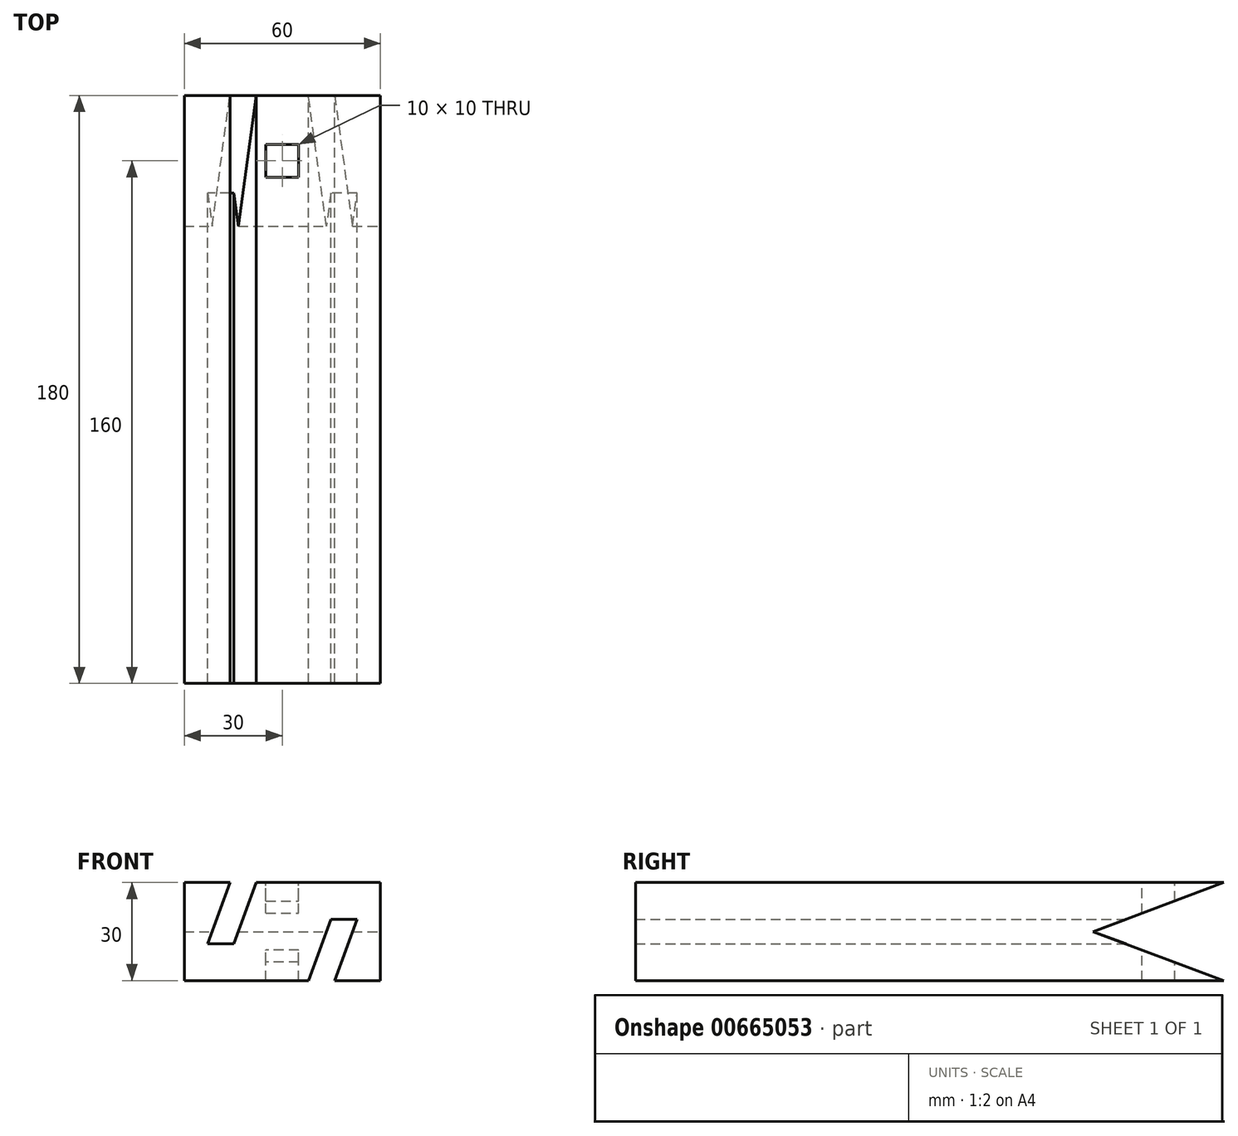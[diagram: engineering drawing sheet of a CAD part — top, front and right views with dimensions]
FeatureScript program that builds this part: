
annotation { "Feature Type Name" : "Feature", "Feature Type Description" : "" }
export const myFeature = defineFeature(function(context is Context, id is Id, definition is map)
    precondition{}
    {
        {
            var Q0;
            Q0=qCreatedBy(makeId("Front.planeOp"),FACE);
            var sketch = newSketch(context, id + "F0", { "sketchPlane" : qUnion([Q0])});
            skLineSegment(sketch, "E0.bottom", {"start": v(30, 15) * mm, "end": v(-30, 15) * mm});
            skLineSegment(sketch, "E0.top", {"start": v(30, -15) * mm, "end": v(-30, -15) * mm});
            skLineSegment(sketch, "E0.left", {"start": v(30, 15) * mm, "end": v(30, -15) * mm});
            skLineSegment(sketch, "E0.right", {"start": v(-30, 15) * mm, "end": v(-30, -15) * mm});
            skLineSegment(sketch, "E1", {"start": v(-8, 15) * mm, "end": v(-14.84, -3.8) * mm});
            skLineSegment(sketch, "E2", {"start": v(-14.84, -3.8) * mm, "end": v(-22.84, -3.8) * mm});
            skLineSegment(sketch, "E3", {"start": v(-22.84, -3.8) * mm, "end": v(-16, 15) * mm});
            skLineSegment(sketch, "E4", {"start": v(16, -15) * mm, "end": v(22.84, 3.8) * mm});
            skLineSegment(sketch, "E5", {"start": v(22.84, 3.8) * mm, "end": v(14.84, 3.8) * mm});
            skLineSegment(sketch, "E6", {"start": v(14.84, 3.8) * mm, "end": v(8, -15) * mm});
            skSolve(sketch);
        }
        {
            var Q0;
            {var subQ3=sQuery(id+"F0.wireOp",EDGE,"E0.left");Q0=makeQuery(id+"F0.imprint","IMPRINT",FACE,{"disambiguationData":[TD([[makeQuery(id+"F0.imprint","IMPRINT",EDGE,{"derivedFrom":subQ3}),-1.0]])]});}
            extrude(context, id + "F1", {"entities" : qUnion([Q0]), "endBound" : BoundingType.SYMMETRIC, "depth" : 320 * mm, "offsetDistance" : 25 * mm});
        }
        {
            var Q0;
            {var subQ0=sQuery(id+"F0.wireOp",EDGE,"E0.bottom");Q0=makeQuery(id+"F1.opExtrude","SWEPT_FACE",FACE,{"disambiguationData":[OSD([subQ0]),TDD([makeQuery(id+"F0.imprint","IMPRINT",EDGE,{"disambiguationData":[TD([[makeQuery(id+"F0.imprint","INTERSECT",VERTEX,{"derivedFrom":[subQ0,sQuery(id+"F0.wireOp",EDGE,"E0.left")]}),-1.0]])],"derivedFrom":subQ0})])]});}
            var sketch = newSketch(context, id + "F2", { "sketchPlane" : qUnion([Q0])});
            skLineSegment(sketch, "E7.bottom", {"start": v(5, 5) * mm, "end": v(-5, 5) * mm});
            skLineSegment(sketch, "E7.top", {"start": v(5, -5) * mm, "end": v(-5, -5) * mm});
            skLineSegment(sketch, "E7.left", {"start": v(5, 5) * mm, "end": v(5, -5) * mm});
            skLineSegment(sketch, "E7.right", {"start": v(-5, 5) * mm, "end": v(-5, -5) * mm});
            skPoint(sketch, "E7.middle", {"position": v(0, 0) * mm});
            skSolve(sketch);
        }
        {
            var Q0;
            Q0=makeQuery(id+"F2.imprint","IMPRINT",FACE,{"disambiguationData":[TD([[makeQuery(id+"F2.imprint","IMPRINT",EDGE,{"derivedFrom":sQuery(id+"F2.wireOp",EDGE,"E7.bottom")}),1.0]])]});
            extrude(context, id + "F3", {"entities" : qUnion([Q0]), "operationType" : NewBodyOperationType.REMOVE, "oppositeDirection" : true, "depth" : 60 * mm, "offsetDistance" : 25 * mm});
        }
        {
            var Q0;
            Q0=makeQuery(id+"F1.opExtrude","SWEPT_FACE",FACE,{"disambiguationData":[OSD([sQuery(id+"F0.wireOp",EDGE,"E0.left")])]});
            var sketch = newSketch(context, id + "F4", { "sketchPlane" : qUnion([Q0])});
            skLineSegment(sketch, "E8", {"start": v(0, 15) * mm, "end": v(0, -15) * mm});
            skLineSegment(sketch, "E9", {"start": v(0, -15) * mm, "end": v(20, -15) * mm});
            skLineSegment(sketch, "E10", {"start": v(20, -15) * mm, "end": v(20, 15) * mm});
            skLineSegment(sketch, "E11", {"start": v(0, 0) * mm, "end": v(-20, 0) * mm});
            skLineSegment(sketch, "E12", {"start": v(-20, 0) * mm, "end": v(20, -15) * mm});
            skLineSegment(sketch, "E13", {"start": v(20, 15) * mm, "end": v(-20, 0) * mm});
            skSolve(sketch);
        }
        {
            var Q0;
            {var subQ5=sQuery(id+"F0.wireOp",EDGE,"E0.left");var subQ8=makeQuery(id+"F1.opExtrude","CAP_EDGE",EDGE,{"disambiguationData":[OSD([subQ5])],"isStart":false});Q0=makeQuery(id+"F4.imprint","IMPRINT",FACE,{"disambiguationData":[TD([[makeQuery(id+"F4.imprint","IMPRINT",EDGE,{"derivedFrom":subQ8}),1.0]])]});}
            var Q1;
            {var subQ0=sQuery(id+"F4.wireOp",EDGE,"E8");var subQ3=sQuery(id+"F4.wireOp",EDGE,"E13");var subQ4=makeQuery(id+"F4.imprint","INTERSECT",VERTEX,{"derivedFrom":[subQ0,subQ3]});Q1=makeQuery(id+"F4.imprint","IMPRINT",FACE,{"disambiguationData":[TD([[makeQuery(id+"F4.imprint","IMPRINT",EDGE,{"disambiguationData":[TD([[subQ4,1.0]])],"derivedFrom":subQ0}),1.0]])]});}
            var Q2;
            {var subQ0=sQuery(id+"F4.wireOp",EDGE,"E9");Q2=makeQuery(id+"F4.imprint","IMPRINT",FACE,{"disambiguationData":[TD([[makeQuery(id+"F4.imprint","IMPRINT",EDGE,{"derivedFrom":subQ0}),1.0]])]});}
            extrude(context, id + "F5", {"entities" : qUnion([Q0, Q1, Q2]), "operationType" : NewBodyOperationType.INTERSECT, "oppositeDirection" : true, "depth" : 60 * mm, "offsetDistance" : 25 * mm});
        }
    });
